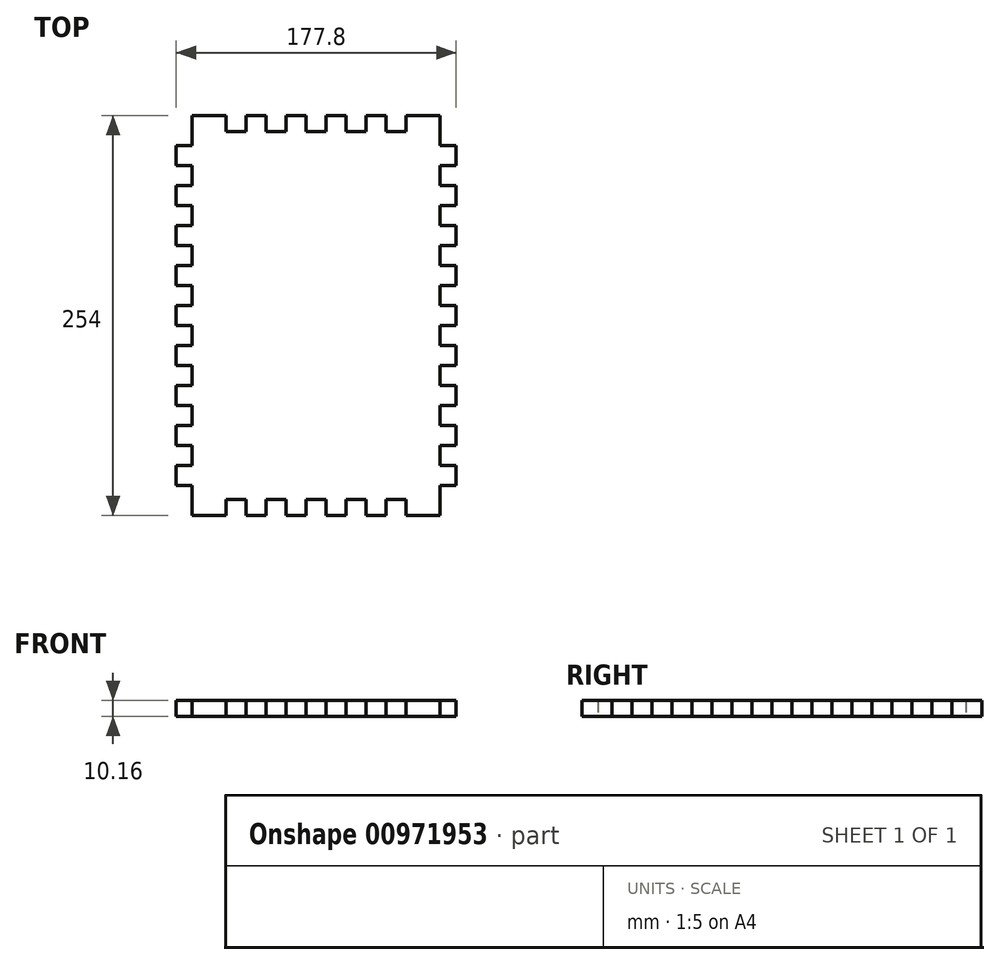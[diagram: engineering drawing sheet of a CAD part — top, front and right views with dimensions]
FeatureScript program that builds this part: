
annotation { "Feature Type Name" : "Feature", "Feature Type Description" : "" }
export const myFeature = defineFeature(function(context is Context, id is Id, definition is map)
    precondition{}
    {
        {
            var Q0;
            Q0=qCreatedBy(makeId("Top.planeOp"),FACE);
            var sketch = newSketch(context, id + "F0", { "sketchPlane" : qUnion([Q0])});
            skLineSegment(sketch, "E0.bottom", {"start": v(10.16, 0) * mm, "end": v(31.75, 0) * mm});
            skLineSegment(sketch, "E0.left", {"start": v(0, -19.05) * mm, "end": v(0, -31.75) * mm});
            skLineSegment(sketch, "E1", {"start": v(10.16, 0) * mm, "end": v(10.16, -19.05) * mm});
            skLineSegment(sketch, "E2", {"start": v(10.16, -19.05) * mm, "end": v(0, -19.05) * mm});
            skLineSegment(sketch, "E3", {"start": v(0, -31.75) * mm, "end": v(10.16, -31.75) * mm});
            skLineSegment(sketch, "E4", {"start": v(10.16, -31.75) * mm, "end": v(10.16, -44.45) * mm});
            skLineSegment(sketch, "E5", {"start": v(10.16, -44.45) * mm, "end": v(0, -44.45) * mm});
            skLineSegment(sketch, "E6", {"start": v(0, -44.45) * mm, "end": v(0, -57.15) * mm});
            skLineSegment(sketch, "E7", {"start": v(0, -57.15) * mm, "end": v(10.16, -57.15) * mm});
            skLineSegment(sketch, "E8", {"start": v(10.16, -57.15) * mm, "end": v(10.16, -69.85) * mm});
            skLineSegment(sketch, "E9", {"start": v(10.16, -69.85) * mm, "end": v(0, -69.85) * mm});
            skLineSegment(sketch, "E10", {"start": v(0, -69.85) * mm, "end": v(0, -82.55) * mm});
            skLineSegment(sketch, "E11", {"start": v(0, -82.55) * mm, "end": v(10.16, -82.55) * mm});
            skLineSegment(sketch, "E12", {"start": v(10.16, -82.55) * mm, "end": v(10.16, -95.25) * mm});
            skLineSegment(sketch, "E13", {"start": v(10.16, -95.25) * mm, "end": v(0, -95.25) * mm});
            skLineSegment(sketch, "E14", {"start": v(0, -95.25) * mm, "end": v(0, -107.95) * mm});
            skLineSegment(sketch, "E15", {"start": v(0, -107.95) * mm, "end": v(10.16, -107.95) * mm});
            skLineSegment(sketch, "E16", {"start": v(10.16, -107.95) * mm, "end": v(10.16, -120.65) * mm});
            skLineSegment(sketch, "E17", {"start": v(10.16, -120.65) * mm, "end": v(0, -120.65) * mm});
            skPoint(sketch, "E18.orphan", {"position": v(0, 0) * mm});
            skLineSegment(sketch, "E19.trimOffspring", {"start": v(0, -120.65) * mm, "end": v(0, -133.35) * mm});
            skLineSegment(sketch, "E20", {"start": v(0, -133.35) * mm, "end": v(10.16, -133.35) * mm});
            skLineSegment(sketch, "E21", {"start": v(10.16, -133.35) * mm, "end": v(10.16, -146.05) * mm});
            skLineSegment(sketch, "E22", {"start": v(10.16, -146.05) * mm, "end": v(0, -146.05) * mm});
            skLineSegment(sketch, "E23.trimOffspring", {"start": v(0, -146.05) * mm, "end": v(0, -158.75) * mm});
            skLineSegment(sketch, "E24", {"start": v(0, -158.75) * mm, "end": v(10.16, -158.75) * mm});
            skLineSegment(sketch, "E25", {"start": v(10.16, -158.75) * mm, "end": v(10.16, -171.45) * mm});
            skLineSegment(sketch, "E26", {"start": v(10.16, -171.45) * mm, "end": v(0, -171.45) * mm});
            skLineSegment(sketch, "E27", {"start": v(0, -171.45) * mm, "end": v(0, -184.15) * mm});
            skLineSegment(sketch, "E28", {"start": v(0, -184.15) * mm, "end": v(10.16, -184.15) * mm});
            skLineSegment(sketch, "E29", {"start": v(10.16, -184.15) * mm, "end": v(10.16, -196.85) * mm});
            skLineSegment(sketch, "E30", {"start": v(10.16, -196.85) * mm, "end": v(0, -196.85) * mm});
            skLineSegment(sketch, "E31", {"start": v(0, -196.85) * mm, "end": v(0, -209.55) * mm});
            skLineSegment(sketch, "E32", {"start": v(0, -209.55) * mm, "end": v(10.16, -209.55) * mm});
            skLineSegment(sketch, "E33", {"start": v(10.16, -209.55) * mm, "end": v(10.16, -222.25) * mm});
            skLineSegment(sketch, "E34", {"start": v(10.16, -222.25) * mm, "end": v(0, -222.25) * mm});
            skLineSegment(sketch, "E35.trimOffspring", {"start": v(0, -222.25) * mm, "end": v(0, -234.95) * mm});
            skLineSegment(sketch, "E36", {"start": v(0, -234.95) * mm, "end": v(10.16, -234.95) * mm});
            skLineSegment(sketch, "E37", {"start": v(10.16, -234.95) * mm, "end": v(10.16, -254) * mm});
            skPoint(sketch, "E38.orphan", {"position": v(0, -254) * mm});
            skLineSegment(sketch, "E39", {"start": v(31.75, 0) * mm, "end": v(31.75, -10.16) * mm});
            skLineSegment(sketch, "E40", {"start": v(31.75, -10.16) * mm, "end": v(44.45, -10.16) * mm});
            skLineSegment(sketch, "E41", {"start": v(44.45, -10.16) * mm, "end": v(44.45, 0) * mm});
            skLineSegment(sketch, "E42", {"start": v(44.45, 0) * mm, "end": v(57.15, 0) * mm});
            skLineSegment(sketch, "E43", {"start": v(57.15, 0) * mm, "end": v(57.15, -10.16) * mm});
            skLineSegment(sketch, "E44", {"start": v(57.15, -10.16) * mm, "end": v(69.85, -10.16) * mm});
            skLineSegment(sketch, "E45", {"start": v(69.85, -10.16) * mm, "end": v(69.85, 0) * mm});
            skLineSegment(sketch, "E46", {"start": v(69.85, 0) * mm, "end": v(82.55, 0) * mm});
            skLineSegment(sketch, "E47", {"start": v(82.55, 0) * mm, "end": v(82.55, -10.16) * mm});
            skLineSegment(sketch, "E48", {"start": v(82.55, -10.16) * mm, "end": v(95.25, -10.16) * mm});
            skLineSegment(sketch, "E49", {"start": v(95.25, -10.16) * mm, "end": v(95.25, 0) * mm});
            skLineSegment(sketch, "E50", {"start": v(95.25, 0) * mm, "end": v(107.95, 0) * mm});
            skLineSegment(sketch, "E51", {"start": v(107.95, 0) * mm, "end": v(107.95, -10.16) * mm});
            skLineSegment(sketch, "E52", {"start": v(107.95, -10.16) * mm, "end": v(120.65, -10.16) * mm});
            skLineSegment(sketch, "E53", {"start": v(120.65, -10.16) * mm, "end": v(120.65, 0) * mm});
            skLineSegment(sketch, "E54", {"start": v(120.65, 0) * mm, "end": v(133.35, 0) * mm});
            skLineSegment(sketch, "E55", {"start": v(133.35, 0) * mm, "end": v(133.35, -10.16) * mm});
            skLineSegment(sketch, "E56", {"start": v(133.35, -10.16) * mm, "end": v(146.05, -10.16) * mm});
            skLineSegment(sketch, "E57", {"start": v(146.05, -10.16) * mm, "end": v(146.05, 0) * mm});
            skLineSegment(sketch, "E58.trimOffspring", {"start": v(146.05, 0) * mm, "end": v(167.64, 0) * mm});
            skLineSegment(sketch, "E59", {"start": v(167.64, 0) * mm, "end": v(167.64, -19.05) * mm});
            skLineSegment(sketch, "E60", {"start": v(167.64, -19.05) * mm, "end": v(167.64, -19.05) * mm});
            skPoint(sketch, "E61.orphan", {"position": v(177.8, 0) * mm});
            skLineSegment(sketch, "E62", {"start": v(88.9, -10.16) * mm, "end": v(88.9, -10.16) * mm});
            skLineSegment(sketch, "E63", {"start": v(0, -127) * mm, "end": v(0, -127) * mm});
            skLineSegment(sketch, "E64.MirrorCS", {"start": v(177.8, -120.65) * mm, "end": v(177.8, -133.35) * mm});
            skLineSegment(sketch, "E65.MirrorCS", {"start": v(177.8, -146.05) * mm, "end": v(177.8, -158.75) * mm});
            skLineSegment(sketch, "E66.MirrorCS", {"start": v(177.8, -69.85) * mm, "end": v(177.8, -82.55) * mm});
            skLineSegment(sketch, "E67.MirrorCS", {"start": v(177.8, -171.45) * mm, "end": v(177.8, -184.15) * mm});
            skLineSegment(sketch, "E68.MirrorCS", {"start": v(177.8, -196.85) * mm, "end": v(177.8, -209.55) * mm});
            skLineSegment(sketch, "E69.MirrorCS", {"start": v(177.8, -44.45) * mm, "end": v(177.8, -57.15) * mm});
            skLineSegment(sketch, "E70.MirrorCS", {"start": v(177.8, -95.25) * mm, "end": v(177.8, -107.95) * mm});
            skLineSegment(sketch, "E71.MirrorCS", {"start": v(177.8, -19.05) * mm, "end": v(177.8, -31.75) * mm});
            skLineSegment(sketch, "E72.MirrorCS", {"start": v(177.8, -222.25) * mm, "end": v(177.8, -234.95) * mm});
            skLineSegment(sketch, "E73.MirrorCS", {"start": v(177.8, -31.75) * mm, "end": v(167.64, -31.75) * mm});
            skLineSegment(sketch, "E74.MirrorCS", {"start": v(167.64, -69.85) * mm, "end": v(177.8, -69.85) * mm});
            skLineSegment(sketch, "E75.MirrorCS", {"start": v(177.8, -158.75) * mm, "end": v(167.64, -158.75) * mm});
            skLineSegment(sketch, "E76.MirrorCS", {"start": v(167.64, -209.55) * mm, "end": v(167.64, -222.25) * mm});
            skLineSegment(sketch, "E77.MirrorCS", {"start": v(167.64, -146.05) * mm, "end": v(177.8, -146.05) * mm});
            skLineSegment(sketch, "E78.MirrorCS", {"start": v(167.64, -82.55) * mm, "end": v(167.64, -95.25) * mm});
            skLineSegment(sketch, "E79.MirrorCS", {"start": v(177.8, -82.55) * mm, "end": v(167.64, -82.55) * mm});
            skLineSegment(sketch, "E80.MirrorCS", {"start": v(167.64, -222.25) * mm, "end": v(177.8, -222.25) * mm});
            skLineSegment(sketch, "E81.MirrorCS", {"start": v(167.64, -95.25) * mm, "end": v(177.8, -95.25) * mm});
            skLineSegment(sketch, "E82.MirrorCS", {"start": v(177.8, -107.95) * mm, "end": v(167.64, -107.95) * mm});
            skLineSegment(sketch, "E83.MirrorCS", {"start": v(177.8, -209.55) * mm, "end": v(167.64, -209.55) * mm});
            skLineSegment(sketch, "E84.MirrorCS", {"start": v(167.64, -57.15) * mm, "end": v(167.64, -69.85) * mm});
            skLineSegment(sketch, "E85.MirrorCS", {"start": v(167.64, -44.45) * mm, "end": v(177.8, -44.45) * mm});
            skLineSegment(sketch, "E86.MirrorCS", {"start": v(167.64, -133.35) * mm, "end": v(167.64, -146.05) * mm});
            skLineSegment(sketch, "E87.MirrorCS", {"start": v(167.64, -19.05) * mm, "end": v(177.8, -19.05) * mm});
            skLineSegment(sketch, "E88.MirrorCS", {"start": v(177.8, -184.15) * mm, "end": v(167.64, -184.15) * mm});
            skLineSegment(sketch, "E89.MirrorCS", {"start": v(177.8, -234.95) * mm, "end": v(167.64, -234.95) * mm});
            skLineSegment(sketch, "E90.MirrorCS", {"start": v(167.64, -120.65) * mm, "end": v(177.8, -120.65) * mm});
            skLineSegment(sketch, "E91.MirrorCS", {"start": v(167.64, -107.95) * mm, "end": v(167.64, -120.65) * mm});
            skLineSegment(sketch, "E92.MirrorCS", {"start": v(167.64, -158.75) * mm, "end": v(167.64, -171.45) * mm});
            skLineSegment(sketch, "E93.MirrorCS", {"start": v(167.64, -184.15) * mm, "end": v(167.64, -196.85) * mm});
            skLineSegment(sketch, "E94.MirrorCS", {"start": v(167.64, -171.45) * mm, "end": v(177.8, -171.45) * mm});
            skLineSegment(sketch, "E95.MirrorCS", {"start": v(177.8, -133.35) * mm, "end": v(167.64, -133.35) * mm});
            skLineSegment(sketch, "E96.MirrorCS", {"start": v(167.64, -31.75) * mm, "end": v(167.64, -44.45) * mm});
            skLineSegment(sketch, "E97.MirrorCS", {"start": v(167.64, -196.85) * mm, "end": v(177.8, -196.85) * mm});
            skLineSegment(sketch, "E98.MirrorCS", {"start": v(177.8, -57.15) * mm, "end": v(167.64, -57.15) * mm});
            skPoint(sketch, "E99.MirrorP", {"position": v(177.8, -254) * mm});
            skLineSegment(sketch, "E100.MirrorCS", {"start": v(167.64, -234.95) * mm, "end": v(167.64, -254) * mm});
            skLineSegment(sketch, "E101.MirrorCS", {"start": v(44.45, -254) * mm, "end": v(57.15, -254) * mm});
            skLineSegment(sketch, "E102.MirrorCS", {"start": v(69.85, -254) * mm, "end": v(82.55, -254) * mm});
            skLineSegment(sketch, "E103.MirrorCS", {"start": v(120.65, -254) * mm, "end": v(133.35, -254) * mm});
            skLineSegment(sketch, "E104.MirrorCS", {"start": v(146.05, -243.84) * mm, "end": v(146.05, -254) * mm});
            skLineSegment(sketch, "E105.MirrorCS", {"start": v(69.85, -243.84) * mm, "end": v(69.85, -254) * mm});
            skLineSegment(sketch, "E106.MirrorCS", {"start": v(133.35, -243.84) * mm, "end": v(146.05, -243.84) * mm});
            skLineSegment(sketch, "E107.MirrorCS", {"start": v(31.75, -243.84) * mm, "end": v(44.45, -243.84) * mm});
            skLineSegment(sketch, "E108.MirrorCS", {"start": v(82.55, -254) * mm, "end": v(82.55, -243.84) * mm});
            skLineSegment(sketch, "E109.MirrorCS", {"start": v(107.95, -243.84) * mm, "end": v(120.65, -243.84) * mm});
            skLineSegment(sketch, "E110.MirrorCS", {"start": v(107.95, -254) * mm, "end": v(107.95, -243.84) * mm});
            skLineSegment(sketch, "E111.MirrorCS", {"start": v(57.15, -254) * mm, "end": v(57.15, -243.84) * mm});
            skLineSegment(sketch, "E112.MirrorCS", {"start": v(120.65, -243.84) * mm, "end": v(120.65, -254) * mm});
            skLineSegment(sketch, "E113.MirrorCS", {"start": v(31.75, -254) * mm, "end": v(31.75, -243.84) * mm});
            skLineSegment(sketch, "E114.MirrorCS", {"start": v(44.45, -243.84) * mm, "end": v(44.45, -254) * mm});
            skLineSegment(sketch, "E115.MirrorCS", {"start": v(95.25, -243.84) * mm, "end": v(95.25, -254) * mm});
            skLineSegment(sketch, "E116.MirrorCS", {"start": v(57.15, -243.84) * mm, "end": v(69.85, -243.84) * mm});
            skLineSegment(sketch, "E117.MirrorCS", {"start": v(133.35, -254) * mm, "end": v(133.35, -243.84) * mm});
            skLineSegment(sketch, "E118.MirrorCS", {"start": v(95.25, -254) * mm, "end": v(107.95, -254) * mm});
            skLineSegment(sketch, "E119.MirrorCS", {"start": v(82.55, -243.84) * mm, "end": v(95.25, -243.84) * mm});
            skLineSegment(sketch, "E120.MirrorCS", {"start": v(146.05, -254) * mm, "end": v(167.64, -254) * mm});
            skLineSegment(sketch, "E121.MirrorCS", {"start": v(10.16, -254) * mm, "end": v(31.75, -254) * mm});
            skSolve(sketch);
        }
        {
            var Q0;
            Q0=makeQuery(id+"F0.imprint","IMPRINT",FACE,{"disambiguationData":[TD([[makeQuery(id+"F0.imprint","IMPRINT",EDGE,{"derivedFrom":sQuery(id+"F0.wireOp",EDGE,"E1")}),1.0]])]});
            extrude(context, id + "F1", {"entities" : qUnion([Q0]), "depth" : 10.16 * mm, "offsetDistance" : 25.4 * mm});
        }
    });
